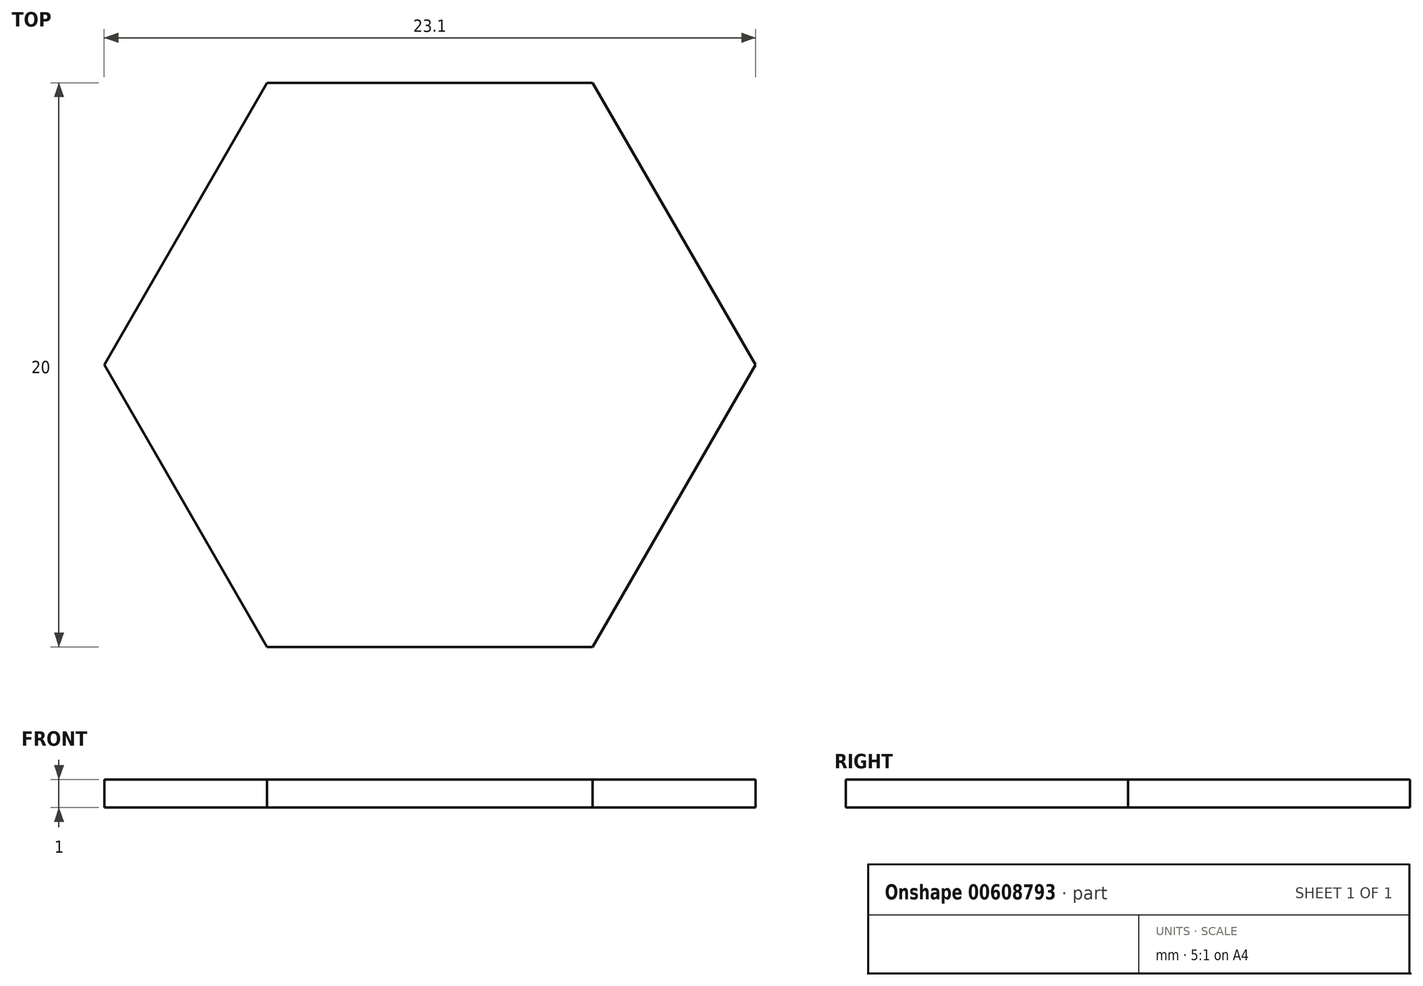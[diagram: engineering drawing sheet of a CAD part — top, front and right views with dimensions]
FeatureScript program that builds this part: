
annotation { "Feature Type Name" : "Feature", "Feature Type Description" : "" }
export const myFeature = defineFeature(function(context is Context, id is Id, definition is map)
    precondition{}
    {
        {
            var Q0;
            Q0=qCreatedBy(makeId("Top.planeOp"),FACE);
            var sketch = newSketch(context, id + "F0", { "sketchPlane" : qUnion([Q0])});
            skCircle(sketch, "E0.cCircle", {"center": v(0, 0) * mm, "radius": 10 * mm, "construction": true});
            skLineSegment(sketch, "E0.0", {"start": v(5.77, -10) * mm, "end": v(-5.77, -10) * mm});
            skLineSegment(sketch, "E0.1", {"start": v(-5.77, -10) * mm, "end": v(-11.55, 0) * mm});
            skLineSegment(sketch, "E0.2", {"start": v(-11.55, 0) * mm, "end": v(-5.77, 10) * mm});
            skLineSegment(sketch, "E0.3", {"start": v(-5.77, 10) * mm, "end": v(5.77, 10) * mm});
            skLineSegment(sketch, "E0.4", {"start": v(5.77, 10) * mm, "end": v(11.55, 0) * mm});
            skLineSegment(sketch, "E0.5", {"start": v(11.55, 0) * mm, "end": v(5.77, -10) * mm});
            skPoint(sketch, "E0.0.midPoint", {"position": v(0, -10) * mm});
            skSolve(sketch);
        }
        {
            var Q0;
            Q0 = qSketchRegion(id + "F0", true);
            extrude(context, id + "F1", {"entities" : qUnion([Q0]), "depth" : 1 * mm, "offsetDistance" : 25 * mm});
        }
    });
